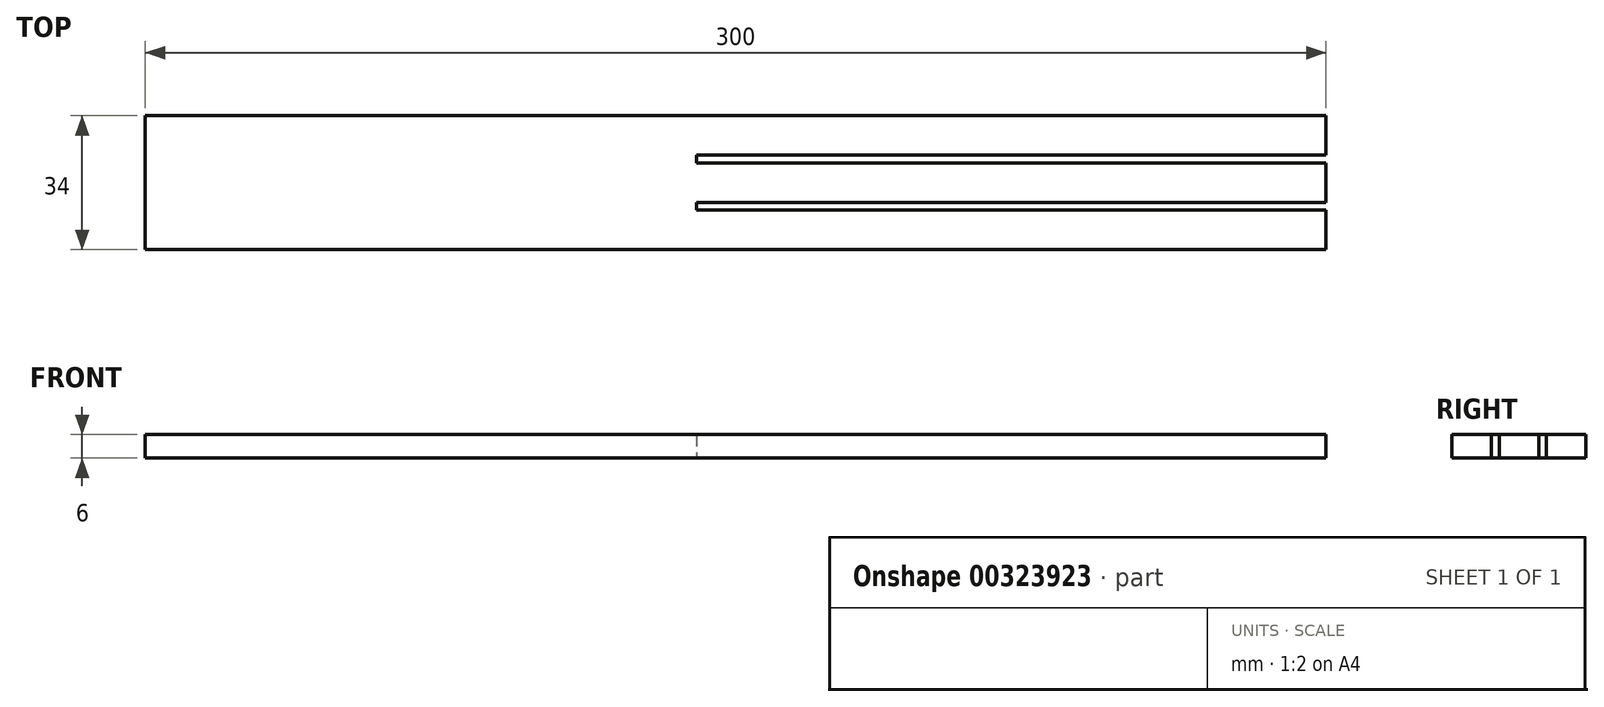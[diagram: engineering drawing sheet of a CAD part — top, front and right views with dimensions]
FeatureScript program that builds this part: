
annotation { "Feature Type Name" : "Feature", "Feature Type Description" : "" }
export const myFeature = defineFeature(function(context is Context, id is Id, definition is map)
    precondition{}
    {
        {
            var Q0;
            Q0=qCreatedBy(makeId("Top.planeOp"),FACE);
            var sketch = newSketch(context, id + "F0", { "sketchPlane" : qUnion([Q0])});
            skLineSegment(sketch, "E0.bottom", {"start": v(-184.7, 34) * mm, "end": v(115.3, 34) * mm});
            skLineSegment(sketch, "E0.top", {"start": v(-184.7, 0) * mm, "end": v(115.3, 0) * mm});
            skLineSegment(sketch, "E0.left", {"start": v(-184.7, 34) * mm, "end": v(-184.7, 0) * mm});
            skLineSegment(sketch, "E0.right", {"start": v(115.3, 34) * mm, "end": v(115.3, 24) * mm});
            skLineSegment(sketch, "E1.bottom", {"start": v(115.3, 24) * mm, "end": v(-44.7, 24) * mm});
            skLineSegment(sketch, "E1.top", {"start": v(115.3, 22) * mm, "end": v(-44.7, 22) * mm});
            skLineSegment(sketch, "E1.right", {"start": v(-44.7, 24) * mm, "end": v(-44.7, 22) * mm});
            skLineSegment(sketch, "E2.bottom", {"start": v(115.3, 10) * mm, "end": v(-44.7, 10) * mm});
            skLineSegment(sketch, "E2.top", {"start": v(115.3, 12) * mm, "end": v(-44.7, 12) * mm});
            skLineSegment(sketch, "E2.right", {"start": v(-44.7, 10) * mm, "end": v(-44.7, 12) * mm});
            skLineSegment(sketch, "E3.trimOffspring", {"start": v(115.3, 22) * mm, "end": v(115.3, 12) * mm});
            skLineSegment(sketch, "E4.trimOffspring", {"start": v(115.3, 10) * mm, "end": v(115.3, 0) * mm});
            skSolve(sketch);
        }
        {
            var Q0;
            Q0=makeQuery(id+"F0.imprint","IMPRINT",FACE,{"disambiguationData":[TD([[makeQuery(id+"F0.imprint","IMPRINT",EDGE,{"derivedFrom":sQuery(id+"F0.wireOp",EDGE,"E0.bottom")}),-1.0]])]});
            extrude(context, id + "F1", {"entities" : qUnion([Q0]), "depth" : 6 * mm});
        }
    });
